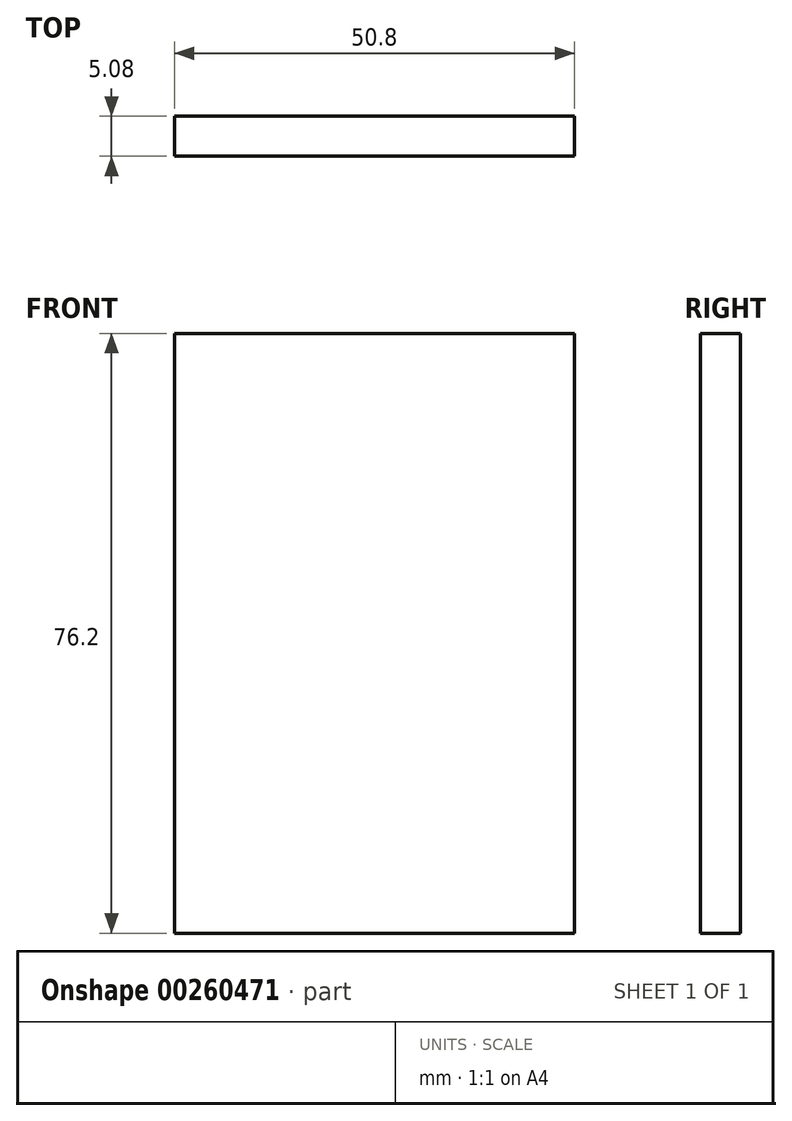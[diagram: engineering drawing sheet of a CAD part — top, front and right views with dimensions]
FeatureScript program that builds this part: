
annotation { "Feature Type Name" : "Feature", "Feature Type Description" : "" }
export const myFeature = defineFeature(function(context is Context, id is Id, definition is map)
    precondition{}
    {
        {
            var Q0;
            Q0=qCreatedBy(makeId("Front.planeOp"),FACE);
            var sketch = newSketch(context, id + "F0", { "sketchPlane" : qUnion([Q0])});
            skLineSegment(sketch, "E0.bottom", {"start": v(25.4, 38.1) * mm, "end": v(-25.4, 38.1) * mm});
            skLineSegment(sketch, "E0.top", {"start": v(25.4, -38.1) * mm, "end": v(-25.4, -38.1) * mm});
            skLineSegment(sketch, "E0.left", {"start": v(25.4, 38.1) * mm, "end": v(25.4, -38.1) * mm});
            skLineSegment(sketch, "E0.right", {"start": v(-25.4, 38.1) * mm, "end": v(-25.4, -38.1) * mm});
            skPoint(sketch, "E0.middle", {"position": v(0, 0) * mm});
            skSolve(sketch);
        }
        {
            var Q0;
            Q0=makeQuery(id+"F0.imprint","IMPRINT",FACE,{"disambiguationData":[TD([[makeQuery(id+"F0.imprint","IMPRINT",EDGE,{"derivedFrom":sQuery(id+"F0.wireOp",EDGE,"E0.bottom")}),1.0]])]});
            extrude(context, id + "F1", {"entities" : qUnion([Q0]), "depth" : 5.08 * mm});
        }
    });
